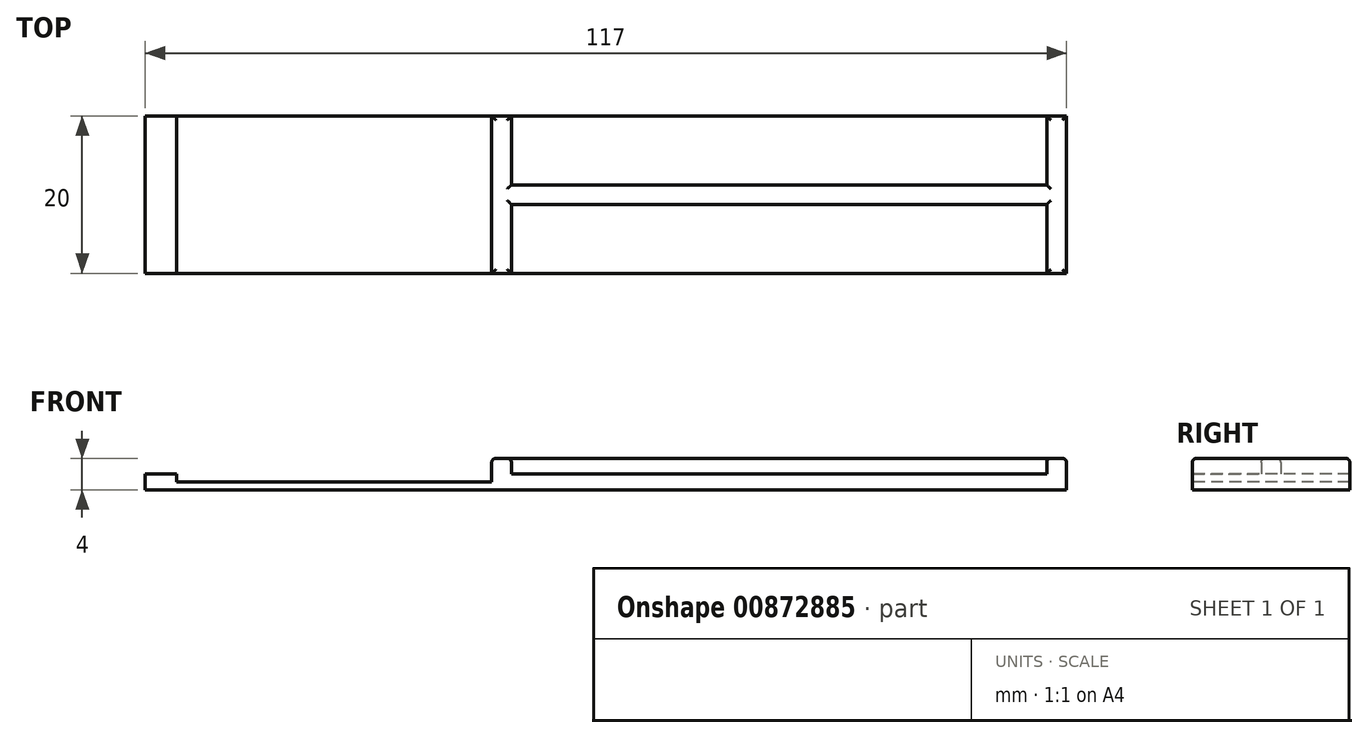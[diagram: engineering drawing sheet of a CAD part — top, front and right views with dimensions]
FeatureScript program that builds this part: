
annotation { "Feature Type Name" : "Feature", "Feature Type Description" : "" }
export const myFeature = defineFeature(function(context is Context, id is Id, definition is map)
    precondition{}
    {
        {
            var Q0;
            Q0=qCreatedBy(makeId("Top.planeOp"),FACE);
            var sketch = newSketch(context, id + "F0", { "sketchPlane" : qUnion([Q0])});
            skLineSegment(sketch, "E0.bottom", {"start": v(-19.35, 6.04) * mm, "end": v(20.65, 6.04) * mm});
            skLineSegment(sketch, "E0.top", {"start": v(-19.35, -13.96) * mm, "end": v(20.65, -13.96) * mm});
            skLineSegment(sketch, "E0.left", {"start": v(-19.35, 6.04) * mm, "end": v(-19.35, -13.96) * mm});
            skLineSegment(sketch, "E0.right", {"start": v(20.65, 6.04) * mm, "end": v(20.65, -13.96) * mm});
            skLineSegment(sketch, "E1.bottom", {"start": v(20.65, -13.96) * mm, "end": v(20.65, -13.96) * mm});
            skLineSegment(sketch, "E1.top", {"start": v(20.65, 6.04) * mm, "end": v(20.65, 6.04) * mm});
            skLineSegment(sketch, "E1.left", {"start": v(20.65, -13.96) * mm, "end": v(20.65, 6.04) * mm});
            skLineSegment(sketch, "E1.right", {"start": v(20.65, -13.96) * mm, "end": v(20.65, 6.04) * mm});
            skLineSegment(sketch, "E2.bottom", {"start": v(20.65, -13.96) * mm, "end": v(93.65, -13.96) * mm});
            skLineSegment(sketch, "E2.top", {"start": v(20.65, 6.04) * mm, "end": v(93.65, 6.04) * mm});
            skLineSegment(sketch, "E2.right", {"start": v(93.65, -13.96) * mm, "end": v(93.65, 6.04) * mm});
            skLineSegment(sketch, "E3.bottom", {"start": v(-19.35, -13.96) * mm, "end": v(-23.35, -13.96) * mm});
            skLineSegment(sketch, "E3.top", {"start": v(-19.35, 6.04) * mm, "end": v(-23.35, 6.04) * mm});
            skLineSegment(sketch, "E3.left", {"start": v(-19.35, -13.96) * mm, "end": v(-19.35, 6.04) * mm});
            skLineSegment(sketch, "E3.right", {"start": v(-23.35, -13.96) * mm, "end": v(-23.35, 6.04) * mm});
            skLineSegment(sketch, "E4.bottom", {"start": v(20.65, 6.04) * mm, "end": v(24.65, 6.04) * mm});
            skLineSegment(sketch, "E4.top", {"start": v(20.65, -13.96) * mm, "end": v(24.65, -13.96) * mm});
            skLineSegment(sketch, "E4.right", {"start": v(24.65, 6.04) * mm, "end": v(24.65, -13.96) * mm});
            skLineSegment(sketch, "E5", {"start": v(24.65, -3.96) * mm, "end": v(93.65, -3.96) * mm, "construction": true});
            skSolve(sketch);
        }
        {
            var Q0;
            Q0=makeQuery(id+"F0.imprint","IMPRINT",FACE,{"disambiguationData":[TD([[makeQuery(id+"F0.imprint","IMPRINT",EDGE,{"derivedFrom":sQuery(id+"F0.wireOp",EDGE,"E0.bottom")}),-1.0]])]});
            extrude(context, id + "F1", {"entities" : qUnion([Q0]), "depth" : 1 * mm, "offsetDistance" : 25 * mm});
        }
        {
            var Q0;
            {var subQ0=sQuery(id+"F0.wireOp",EDGE,"E0.right");Q0=makeQuery(id+"F0.imprint","IMPRINT",FACE,{"disambiguationData":[TD([[makeQuery(id+"F0.imprint","IMPRINT",EDGE,{"derivedFrom":subQ0}),1.0]])]});}
            var Q1;
            Q1=makeQuery(id+"F0.imprint","IMPRINT",FACE,{"disambiguationData":[TD([[makeQuery(id+"F0.imprint","IMPRINT",EDGE,{"derivedFrom":sQuery(id+"F0.wireOp",EDGE,"E0.left")}),-1.0]])]});
            var Q2;
            {var subQ2=sQuery(id+"F0.wireOp",EDGE,"E2.right");Q2=makeQuery(id+"F0.imprint","IMPRINT",FACE,{"disambiguationData":[TD([[makeQuery(id+"F0.imprint","IMPRINT",EDGE,{"derivedFrom":subQ2}),1.0]])]});}
            extrude(context, id + "F2", {"entities" : qUnion([Q0, Q1, Q2]), "operationType" : NewBodyOperationType.ADD, "depth" : 2 * mm, "offsetDistance" : 25 * mm});
        }
        {
            var Q0;
            Q0=makeQuery(id+"F2.opExtrude","CAP_FACE",FACE,{"disambiguationData":[OSD([sQuery(id+"F0.wireOp",EDGE,"E0.right"),sQuery(id+"F0.wireOp",EDGE,"E2.bottom"),sQuery(id+"F0.wireOp",EDGE,"E2.top"),sQuery(id+"F0.wireOp",EDGE,"E2.right")])],"isStart":false});
            var sketch = newSketch(context, id + "F3", { "sketchPlane" : qUnion([Q0])});
            skLineSegment(sketch, "E6", {"start": v(20.65, -13.96) * mm, "end": v(20.65, 6.04) * mm});
            skLineSegment(sketch, "E7", {"start": v(20.65, 6.04) * mm, "end": v(23.15, 6.04) * mm});
            skLineSegment(sketch, "E8", {"start": v(23.15, 6.04) * mm, "end": v(23.15, -2.71) * mm});
            skLineSegment(sketch, "E9", {"start": v(23.15, -2.71) * mm, "end": v(91.15, -2.71) * mm});
            skLineSegment(sketch, "E10", {"start": v(91.15, -2.71) * mm, "end": v(91.15, 6.04) * mm});
            skLineSegment(sketch, "E11", {"start": v(91.15, 6.04) * mm, "end": v(93.65, 6.04) * mm});
            skLineSegment(sketch, "E12", {"start": v(93.65, 6.04) * mm, "end": v(93.65, -13.96) * mm});
            skLineSegment(sketch, "E13", {"start": v(93.65, -13.96) * mm, "end": v(91.15, -13.96) * mm});
            skLineSegment(sketch, "E14", {"start": v(91.15, -13.96) * mm, "end": v(91.15, -5.21) * mm});
            skLineSegment(sketch, "E15", {"start": v(91.15, -5.21) * mm, "end": v(23.15, -5.21) * mm});
            skLineSegment(sketch, "E16", {"start": v(23.15, -5.21) * mm, "end": v(23.15, -13.96) * mm});
            skLineSegment(sketch, "E17", {"start": v(23.15, -13.96) * mm, "end": v(20.65, -13.96) * mm});
            skSolve(sketch);
        }
        {
            var Q0;
            Q0 = qSketchRegion(id + "F3", true);
            extrude(context, id + "F4", {"entities" : qUnion([Q0]), "operationType" : NewBodyOperationType.ADD, "depth" : 2 * mm, "offsetDistance" : 25 * mm});
        }
        {
            var Q0;
            Q0=makeQuery(id+"F4.opExtrude","CAP_FACE",FACE,{"disambiguationData":[OSD([sQuery(id+"F3.wireOp",EDGE,"E6"),sQuery(id+"F3.wireOp",EDGE,"E7"),sQuery(id+"F3.wireOp",EDGE,"E8"),sQuery(id+"F3.wireOp",EDGE,"E9"),sQuery(id+"F3.wireOp",EDGE,"E10"),sQuery(id+"F3.wireOp",EDGE,"E11"),sQuery(id+"F3.wireOp",EDGE,"E12"),sQuery(id+"F3.wireOp",EDGE,"E13"),sQuery(id+"F3.wireOp",EDGE,"E14"),sQuery(id+"F3.wireOp",EDGE,"E15"),sQuery(id+"F3.wireOp",EDGE,"E16"),sQuery(id+"F3.wireOp",EDGE,"E17")])],"isStart":false});
            fillet(context, id + "F5", {"entities" : qUnion([Q0]), "radius" : 0.5 * mm, "tangentPropagation" : true, "allowEdgeOverflow" : false});
        }
    });
